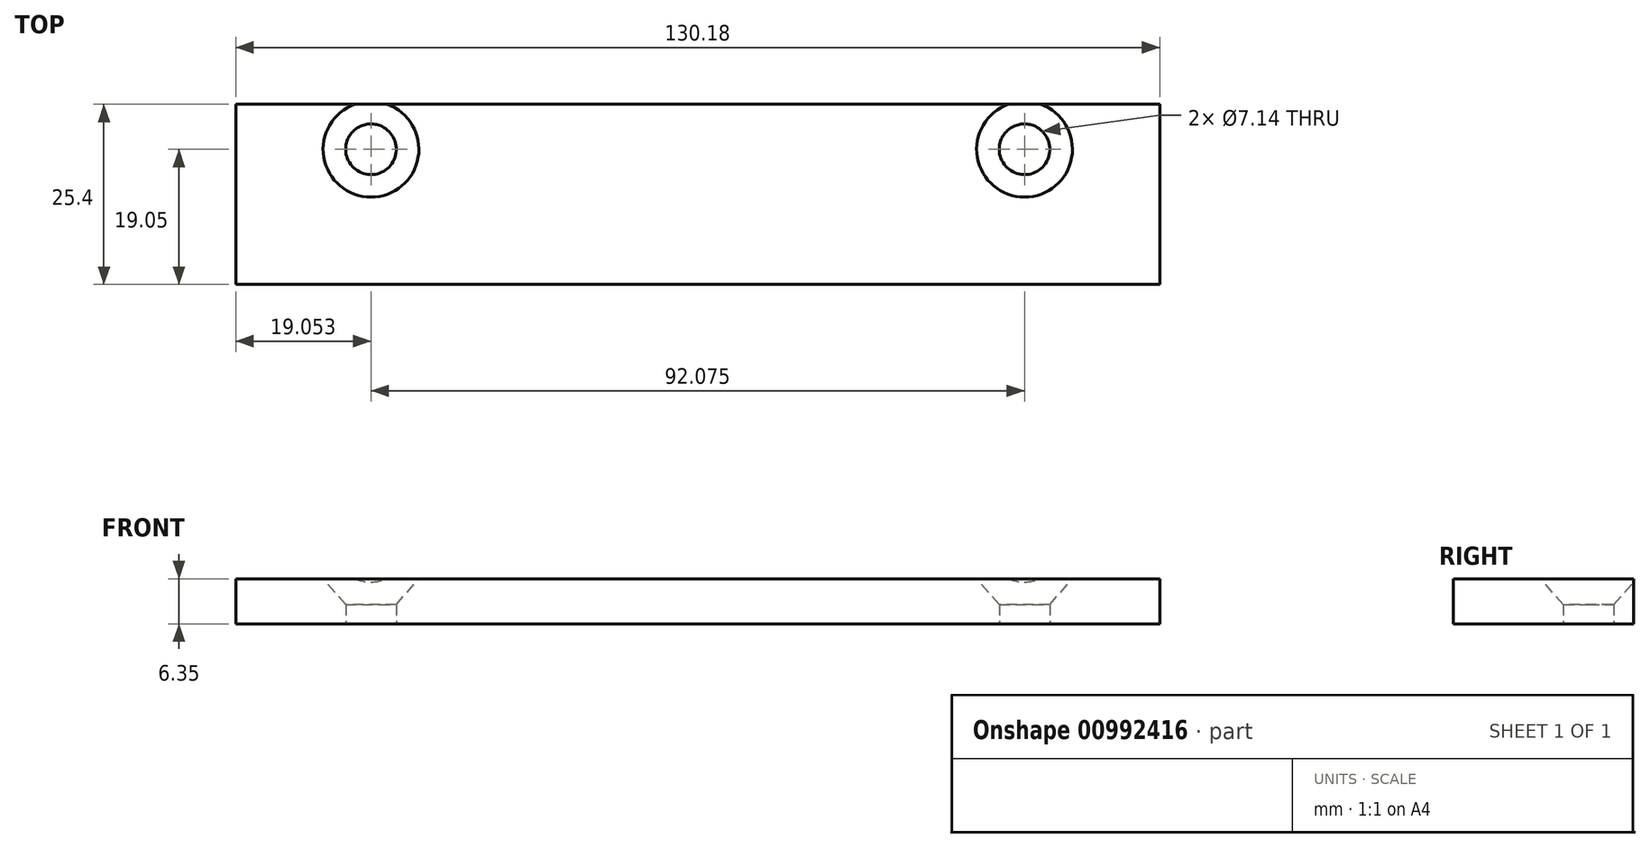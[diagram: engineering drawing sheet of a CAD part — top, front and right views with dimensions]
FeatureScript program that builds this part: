
annotation { "Feature Type Name" : "Feature", "Feature Type Description" : "" }
export const myFeature = defineFeature(function(context is Context, id is Id, definition is map)
    precondition{}
    {
        {
            var Q0;
            Q0=qCreatedBy(makeId("Top.planeOp"),FACE);
            var sketch = newSketch(context, id + "F0", { "sketchPlane" : qUnion([Q0])});
            skLineSegment(sketch, "E0.bottom", {"start": v(65.09, 12.7) * mm, "end": v(-65.09, 12.7) * mm});
            skLineSegment(sketch, "E0.top", {"start": v(65.09, -12.7) * mm, "end": v(-65.09, -12.7) * mm});
            skLineSegment(sketch, "E0.left", {"start": v(65.09, 12.7) * mm, "end": v(65.09, -12.7) * mm});
            skLineSegment(sketch, "E0.right", {"start": v(-65.09, 12.7) * mm, "end": v(-65.09, -12.7) * mm});
            skPoint(sketch, "E0.middle", {"position": v(0, 0) * mm});
            skPoint(sketch, "E1", {"position": v(-46.04, 6.35) * mm});
            skPoint(sketch, "E2", {"position": v(46.04, 6.35) * mm});
            skSolve(sketch);
        }
        {
            var Q0;
            Q0=makeQuery(id+"F0.imprint","IMPRINT",FACE,{"disambiguationData":[TD([[makeQuery(id+"F0.imprint","IMPRINT",EDGE,{"derivedFrom":sQuery(id+"F0.wireOp",EDGE,"E0.bottom")}),1.0]])]});
            extrude(context, id + "F1", {"entities" : qUnion([Q0]), "oppositeDirection" : true, "depth" : 6.35 * mm, "offsetDistance" : 25.4 * mm});
        }
        {
            var Q0;
            Q0=sQuery(id+"F0.wireOp",VERTEX,"E1");
            var Q1;
            Q1=sQuery(id+"F0.wireOp",VERTEX,"E2");
            var Q2;
            Q2=makeQuery(id+"F1.opExtrude","SWEPT_BODY",BODY,{"disambiguationData":[OSD([sQuery(id+"F0.wireOp",EDGE,"E0.bottom"),sQuery(id+"F0.wireOp",EDGE,"E0.top"),sQuery(id+"F0.wireOp",EDGE,"E0.left"),sQuery(id+"F0.wireOp",EDGE,"E0.right")])]});
            hole(context, id + "F2", {"style" : HoleStyle.C_SINK, "endStyle" : HoleEndStyle.BLIND, "standardTappedOrClearance" : lookupTablePath({ "fit" : "Normal (ASME)", "standard" : "ANSI", "size" : "1/4", "type" : "Clearance" }), "standardBlindInLast" : lookupTablePath({ "fit" : "Normal", "standard" : "ANSI", "engagement" : "75%", "pitch" : "20 tpi", "size" : "1/4", "type" : "Clearance & tapped" }), "holeDiameter" : 7.14 * mm, "cSinkDiameter" : 13.5 * mm, "cSinkAngle" : 82 * degree, "majorDiameter" : 6.35 * mm, "holeDepth" : 29.63 * mm, "isTappedThrough" : true, "tappedDepth" : 25.4 * mm, "tapClearance" : 3, "locations" : qUnion([Q0, Q1]), "scope" : qUnion([Q2]), "startStyle" : HoleStartStyle.SKETCH});
        }
    });
